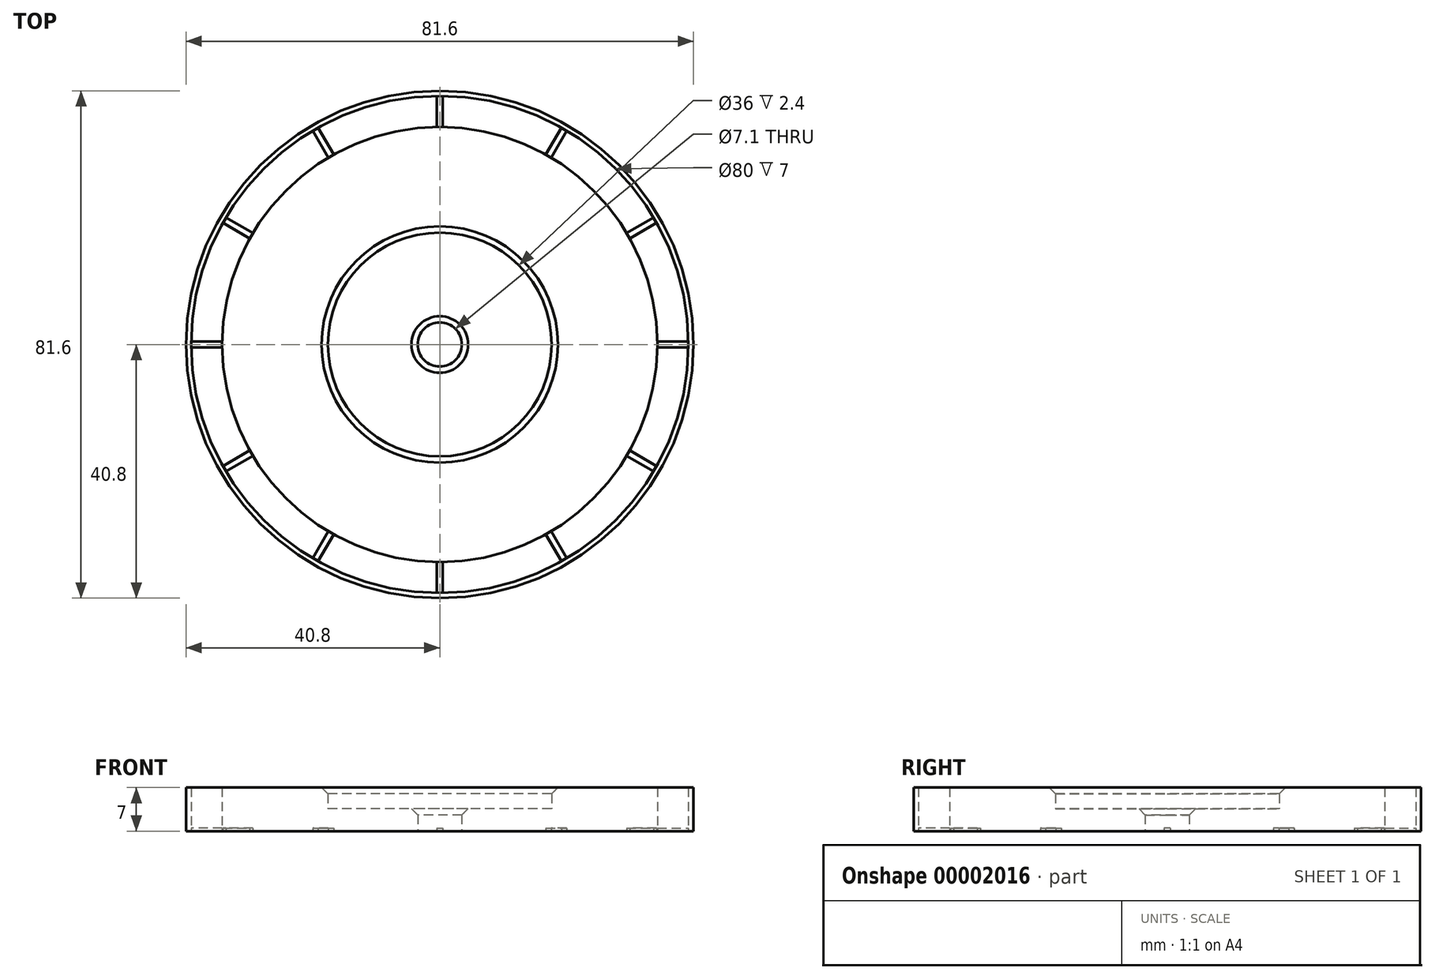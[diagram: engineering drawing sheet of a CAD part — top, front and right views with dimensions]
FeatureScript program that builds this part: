
annotation { "Feature Type Name" : "Feature", "Feature Type Description" : "" }
export const myFeature = defineFeature(function(context is Context, id is Id, definition is map)
    precondition{}
    {
        {
            var Q0;
            Q0=qCreatedBy(makeId("Top.planeOp"),FACE);
            var sketch = newSketch(context, id + "F0", { "sketchPlane" : qUnion([Q0])});
            skCircle(sketch, "E0", {"center": v(0, 0) * mm, "radius": 35 * mm});
            skCircle(sketch, "E1", {"center": v(0, 0) * mm, "radius": 40 * mm});
            skCircle(sketch, "E2", {"center": v(0, 0) * mm, "radius": 40.8 * mm});
            skCircle(sketch, "E3", {"center": v(0, 0) * mm, "radius": 18 * mm});
            skCircle(sketch, "E4", {"center": v(0, 0) * mm, "radius": 3.55 * mm});
            skSolve(sketch);
        }
        {
            var Q0;
            Q0=makeQuery(id+"F0.imprint","IMPRINT",FACE,{"disambiguationData":[TD([[makeQuery(id+"F0.imprint","IMPRINT",EDGE,{"derivedFrom":sQuery(id+"F0.wireOp",EDGE,"E0")}),1.0]])]});
            var Q1;
            Q1=makeQuery(id+"F0.imprint","IMPRINT",FACE,{"disambiguationData":[TD([[makeQuery(id+"F0.imprint","IMPRINT",EDGE,{"derivedFrom":sQuery(id+"F0.wireOp",EDGE,"E1")}),-1.0]])]});
            extrude(context, id + "F1", {"entities" : qUnion([Q0, Q1]), "flatOperationType" : FlatOperationType.REMOVE, "depth" : 7 * mm, "offsetDistance" : 25 * mm, "domain" : OperationDomain.MODEL});
        }
        {
            var Q0;
            Q0=makeQuery(id+"F0.imprint","IMPRINT",FACE,{"disambiguationData":[TD([[makeQuery(id+"F0.imprint","IMPRINT",EDGE,{"derivedFrom":sQuery(id+"F0.wireOp",EDGE,"E3")}),1.0]])]});
            extrude(context, id + "F2", {"entities" : qUnion([Q0]), "operationType" : NewBodyOperationType.ADD, "flatOperationType" : FlatOperationType.REMOVE, "depth" : (7 - 3.4) * mm, "offsetDistance" : 25 * mm, "domain" : OperationDomain.MODEL});
        }
        {
            var Q0;
            {var subQ0=sQuery(id+"F0.wireOp",EDGE,"E3");Q0=makeQuery(id+"F2.boolean.opBoolean","MERGE",FACE,{"derivedFrom":[makeQuery(id+"F1.opExtrude","CAP_FACE",FACE,{"disambiguationData":[OSD([sQuery(id+"F0.wireOp",EDGE,"E0"),subQ0])],"isStart":true}),makeQuery(id+"F2.opExtrude","CAP_FACE",FACE,{"disambiguationData":[OSD([subQ0,sQuery(id+"F0.wireOp",EDGE,"E4")])],"isStart":true})]});}
            var sketch = newSketch(context, id + "F3", { "sketchPlane" : qUnion([Q0])});
            skLineSegment(sketch, "E5", {"start": v(0, 0) * mm, "end": v(0, 38.64) * mm, "construction": true});
            skLineSegment(sketch, "E6", {"start": v(-0.5, 35) * mm, "end": v(-0.5, 40) * mm});
            skLineSegment(sketch, "E7", {"start": v(-0.5, 40) * mm, "end": v(0.5, 40) * mm});
            skLineSegment(sketch, "E8", {"start": v(0.5, 40) * mm, "end": v(0.5, 35) * mm});
            skPoint(sketch, "E9", {"position": v(0, 40) * mm});
            skCircle(sketch, "E10.0", {"center": v(0, 0) * mm, "radius": 40 * mm, "construction": true});
            skSolve(sketch);
        }
        {
            var Q0;
            {var subQ2=sQuery(id+"F3.wireOp",EDGE,"E6");Q0=makeQuery(id+"F3.imprint","IMPRINT",FACE,{"disambiguationData":[TD([[makeQuery(id+"F3.imprint","IMPRINT",EDGE,{"derivedFrom":subQ2}),-1.0]])]});}
            var Q1;
            Q1=makeQuery(id+"F1.opExtrude","CAP_FACE",FACE,{"disambiguationData":[OSD([sQuery(id+"F0.wireOp",EDGE,"E0"),sQuery(id+"F0.wireOp",EDGE,"E3")])],"isStart":false});
            extrude(context, id + "F4", {"entities" : qUnion([Q0]), "oppositeDirection" : true, "endBoundEntity" : qUnion([Q1]), "depth" : .5 * mm});
        }
        {
            var Q0;
            Q0=makeQuery(id+"F4.opExtrude","SWEPT_BODY",BODY,{"disambiguationData":[OSD([sQuery(id+"F0.wireOp",EDGE,"E0"),sQuery(id+"F3.wireOp",EDGE,"E6"),sQuery(id+"F3.wireOp",EDGE,"E7"),sQuery(id+"F3.wireOp",EDGE,"E8")])]});
            var Q1;
            Q1=makeQuery(id+"F1.opExtrude","SWEPT_FACE",FACE,{"disambiguationData":[OSD([sQuery(id+"F0.wireOp",EDGE,"E3")])]});
            circularPattern(context, id + "F5", {"entities" : qUnion([Q0]), "axis" : qUnion([Q1]), "angle" : 360 * degree, "instanceCount" : 12, "equalSpace" : true});
        }
        {
            var Q0;
            Q0=makeQuery(id+"F1.opExtrude","CAP_EDGE",EDGE,{"disambiguationData":[OSD([sQuery(id+"F0.wireOp",EDGE,"E3")])],"isStart":false});
            chamfer(context, id + "F6", {"entities" : qUnion([Q0]), "width" : 1 * mm, "tangentPropagation" : true});
        }
        {
            var Q0;
            Q0=makeQuery(id+"F2.opExtrude","CAP_EDGE",EDGE,{"disambiguationData":[OSD([sQuery(id+"F0.wireOp",EDGE,"E4")])],"isStart":false});
            chamfer(context, id + "F7", {"entities" : qUnion([Q0]), "width" : 1 * mm, "tangentPropagation" : true});
        }
        {
            var Q0;
            Q0=makeQuery(id+"F1.opExtrude","CAP_FACE",FACE,{"disambiguationData":[OSD([sQuery(id+"F0.wireOp",EDGE,"E0"),sQuery(id+"F0.wireOp",EDGE,"E3")])],"isStart":false});
            extrude(context, id + "F8", {"entities" : qUnion([Q0]), "operationType" : NewBodyOperationType.REMOVE, "depth" : 4 * mm});
        }
    });
